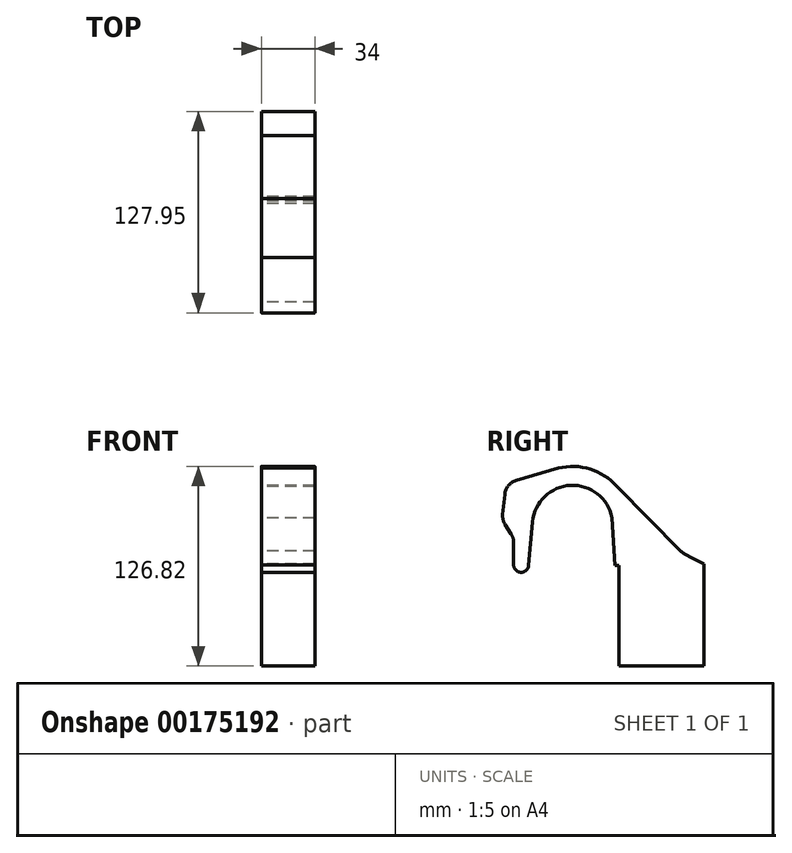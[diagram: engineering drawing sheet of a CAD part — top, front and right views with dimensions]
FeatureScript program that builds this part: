
annotation { "Feature Type Name" : "Feature", "Feature Type Description" : "" }
export const myFeature = defineFeature(function(context is Context, id is Id, definition is map)
    precondition{}
    {
        {
            var Q0;
            Q0=qCreatedBy(makeId("Right.planeOp"),FACE);
            var sketch = newSketch(context, id + "F0", { "sketchPlane" : qUnion([Q0])});
            skArc(sketch, "E0.1", {"start": v(-64.13, 1811.87) * mm, "mid": v(-43.9, 1811.32) * mm, "end": v(-26.9, 1800.32) * mm});
            skLineSegment(sketch, "E0.2", {"start": v(-64.13, 1811.87) * mm, "end": v(-90.98, 1803.96) * mm});
            skArc(sketch, "E0.3", {"start": v(-98.1, 1795.34) * mm, "mid": v(-95.86, 1800.74) * mm, "end": v(-90.98, 1803.96) * mm});
            skLineSegment(sketch, "E0.4", {"start": v(-98.1, 1795.34) * mm, "end": v(-99.37, 1782.4) * mm});
            skLineSegment(sketch, "E0.5", {"start": v(-92.46, 1764.74) * mm, "end": v(-92.46, 1750.3) * mm});
            skLineSegment(sketch, "E0.6", {"start": v(-80.39, 1777.88) * mm, "end": v(-83, 1750) * mm});
            skArc(sketch, "E0.7", {"start": v(-80.39, 1777.88) * mm, "mid": v(-56.28, 1800.97) * mm, "end": v(-29.98, 1780.41) * mm});
            skLineSegment(sketch, "E0.8", {"start": v(-29.98, 1780.41) * mm, "end": v(-28.26, 1750) * mm});
            skPoint(sketch, "E0.9", {"position": v(9.35, 1759.29) * mm});
            skLineSegment(sketch, "E0.10", {"start": v(28.53, 1751.18) * mm, "end": v(28.53, 1686.18) * mm});
            skLineSegment(sketch, "E0.11", {"start": v(-25.47, 1686.18) * mm, "end": v(-25.47, 1750) * mm});
            skLineSegment(sketch, "E0.12", {"start": v(-97.83, 1776.03) * mm, "end": v(-94.05, 1770.16) * mm});
            skPoint(sketch, "E0.13", {"position": v(-95.86, 1800.74) * mm});
            skPoint(sketch, "E0.14", {"position": v(-98.74, 1788.88) * mm});
            skPoint(sketch, "E0.15", {"position": v(-81.7, 1763.94) * mm});
            skPoint(sketch, "E0.16", {"position": v(22.54, 1754.03) * mm});
            skLineSegment(sketch, "E1", {"start": v(28.53, 1751.18) * mm, "end": v(22.54, 1754.03) * mm});
            skArc(sketch, "E2", {"start": v(13.35, 1759.29) * mm, "mid": v(17.84, 1756.48) * mm, "end": v(22.54, 1754.03) * mm});
            skArc(sketch, "E3", {"start": v(-99.37, 1782.4) * mm, "mid": v(-99.14, 1779.09) * mm, "end": v(-97.83, 1776.03) * mm});
            skArc(sketch, "E4", {"start": v(-92.46, 1764.74) * mm, "mid": v(-92.87, 1767.56) * mm, "end": v(-94.05, 1770.16) * mm});
            skArc(sketch, "E5", {"start": v(-92.46, 1750.3) * mm, "mid": v(-87.87, 1745.7) * mm, "end": v(-83, 1750) * mm});
            skLineSegment(sketch, "E6", {"start": v(28.53, 1686.18) * mm, "end": v(-25.47, 1686.18) * mm});
            skLineSegment(sketch, "E7", {"start": v(-28.26, 1750) * mm, "end": v(-25.47, 1750) * mm});
            skLineSegment(sketch, "E8", {"start": v(-26.9, 1800.32) * mm, "end": v(13.35, 1759.29) * mm});
            skSolve(sketch);
        }
        {
            var Q0;
            Q0=qSketchRegion(id+"F0",true);
            extrude(context, id + "F1", {"entities" : qUnion([Q0]), "depth" : 34 * mm});
        }
    });
